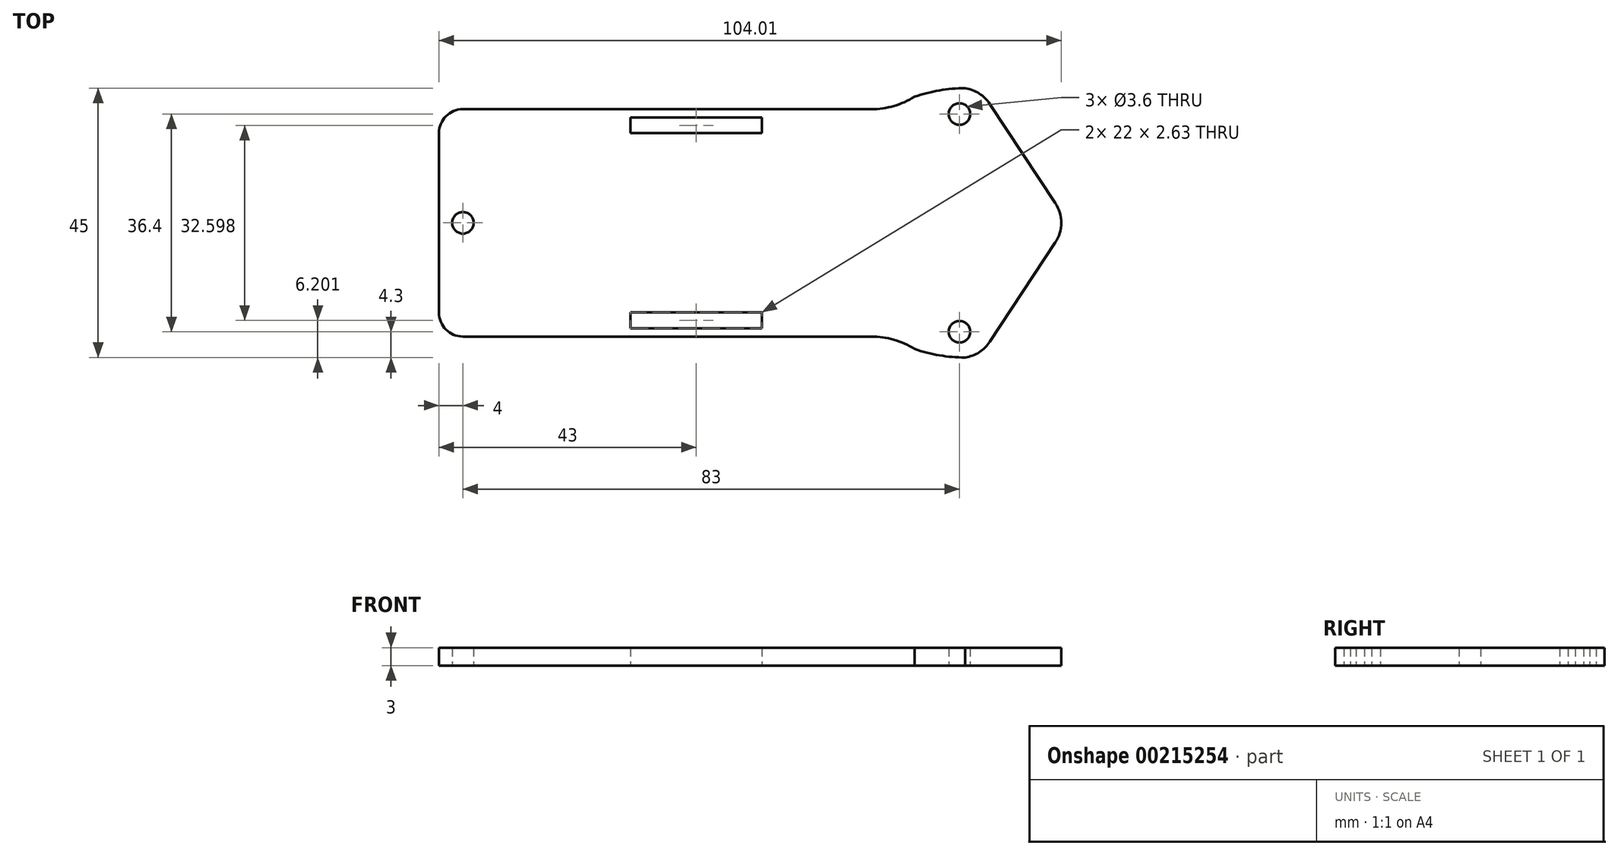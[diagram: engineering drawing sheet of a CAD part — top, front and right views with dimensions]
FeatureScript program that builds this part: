
annotation { "Feature Type Name" : "Feature", "Feature Type Description" : "" }
export const myFeature = defineFeature(function(context is Context, id is Id, definition is map)
    precondition{}
    {
        {
            var Q0;
            Q0=qCreatedBy(makeId("Top.planeOp"),FACE);
            var sketch = newSketch(context, id + "F0", { "sketchPlane" : qUnion([Q0])});
            skLineSegment(sketch, "E0.bottom", {"start": v(-18.2, -18.2) * mm, "end": v(18.2, -18.2) * mm, "construction": true});
            skLineSegment(sketch, "E0.top", {"start": v(-18.2, 18.2) * mm, "end": v(18.2, 18.2) * mm, "construction": true});
            skLineSegment(sketch, "E0.left", {"start": v(-18.2, -18.2) * mm, "end": v(-18.2, 18.2) * mm, "construction": true});
            skLineSegment(sketch, "E0.right", {"start": v(18.2, -18.2) * mm, "end": v(18.2, 18.2) * mm, "construction": true});
            skPoint(sketch, "E0.middle", {"position": v(0, 0) * mm});
            skCircle(sketch, "E1", {"center": v(-18.2, 18.2) * mm, "radius": 1.8 * mm});
            skCircle(sketch, "E2.MirrorC", {"center": v(-18.2, -18.2) * mm, "radius": 1.8 * mm});
            skPoint(sketch, "E3.right.end.orphan", {"position": v(80.8, 22.5) * mm});
            skPoint(sketch, "E4.orphan", {"position": v(80.8, -22.5) * mm});
            skLineSegment(sketch, "E5", {"start": v(-101.2, 19) * mm, "end": v(-70.85, 19) * mm});
            skLineSegment(sketch, "E6.MirrorCS", {"start": v(-101.2, -19) * mm, "end": v(-70.85, -19) * mm});
            skPoint(sketch, "E7.orphan", {"position": v(-80.8, 22.5) * mm});
            skPoint(sketch, "E8.orphan", {"position": v(-80.8, -22.5) * mm});
            skLineSegment(sketch, "E9.bottom", {"start": v(-73.2, -17.61) * mm, "end": v(-51.2, -17.61) * mm});
            skLineSegment(sketch, "E9.top", {"start": v(-73.2, -14.99) * mm, "end": v(-51.2, -14.99) * mm});
            skLineSegment(sketch, "E9.left", {"start": v(-73.2, -17.61) * mm, "end": v(-73.2, -14.99) * mm});
            skLineSegment(sketch, "E9.right", {"start": v(-51.2, -17.61) * mm, "end": v(-51.2, -14.99) * mm});
            skPoint(sketch, "E9.middle", {"position": v(-62.2, -16.3) * mm});
            skLineSegment(sketch, "E10.MirrorCS", {"start": v(-73.2, 14.99) * mm, "end": v(-51.2, 14.99) * mm});
            skLineSegment(sketch, "E11.MirrorCS", {"start": v(-73.2, 17.61) * mm, "end": v(-51.2, 17.61) * mm});
            skLineSegment(sketch, "E12.MirrorCS", {"start": v(-51.2, 17.61) * mm, "end": v(-51.2, 14.99) * mm});
            skLineSegment(sketch, "E13.MirrorCS", {"start": v(-73.2, 17.61) * mm, "end": v(-73.2, 14.99) * mm});
            skLineSegment(sketch, "E14", {"start": v(-105.2, 15) * mm, "end": v(-105.2, -15) * mm});
            skPoint(sketch, "E15.visualSharp", {"position": v(-105.2, 19) * mm});
            skArc(sketch, "E15.filletArc", {"start": v(-101.2, 19) * mm, "mid": v(-104.03, 17.83) * mm, "end": v(-105.2, 15) * mm});
            skPoint(sketch, "E16.visualSharp", {"position": v(-105.2, -19) * mm});
            skArc(sketch, "E16.filletArc", {"start": v(-105.2, -15) * mm, "mid": v(-104.03, -17.83) * mm, "end": v(-101.2, -19) * mm});
            skCircle(sketch, "E17", {"center": v(-101.2, 0) * mm, "radius": 1.8 * mm});
            skPoint(sketch, "E17.centerSnap0", {"position": v(-105.2, 0) * mm});
            skLineSegment(sketch, "E18", {"start": v(-70.85, 19) * mm, "end": v(-32.93, 19) * mm});
            skArc(sketch, "E19", {"start": v(-32.93, 19) * mm, "mid": v(-29.17, 19.53) * mm, "end": v(-25.7, 21.08) * mm});
            skArc(sketch, "E20", {"start": v(-17.27, 22.5) * mm, "mid": v(-21.55, 22.14) * mm, "end": v(-25.7, 21.08) * mm});
            skArc(sketch, "E21.MirrorCS", {"start": v(-32.93, -19) * mm, "mid": v(-29.17, -19.53) * mm, "end": v(-25.7, -21.08) * mm});
            skArc(sketch, "E22.MirrorCS", {"start": v(-17.27, -22.5) * mm, "mid": v(-21.55, -22.14) * mm, "end": v(-25.7, -21.08) * mm});
            skLineSegment(sketch, "E23", {"start": v(-70.85, -19) * mm, "end": v(-32.93, -19) * mm});
            skLineSegment(sketch, "E24", {"start": v(-51.2, 14.99) * mm, "end": v(-51.2, -14.99) * mm, "construction": true});
            skLineSegment(sketch, "E25", {"start": v(-105.2, 0) * mm, "end": v(-0.2, 0) * mm, "construction": true});
            skLineSegment(sketch, "E26", {"start": v(-13.12, 19.87) * mm, "end": v(-2.18, 3.3) * mm});
            skLineSegment(sketch, "E27.MirrorCS", {"start": v(-13.12, -19.87) * mm, "end": v(-2.18, -3.3) * mm});
            skArc(sketch, "E28", {"start": v(-13.12, 19.87) * mm, "mid": v(-14.91, 21.63) * mm, "end": v(-17.27, 22.5) * mm});
            skArc(sketch, "E29.MirrorCS", {"start": v(-13.12, -19.87) * mm, "mid": v(-14.91, -21.63) * mm, "end": v(-17.27, -22.5) * mm});
            skArc(sketch, "E30.filletArc", {"start": v(-2.18, -3.3) * mm, "mid": v(-1.19, 0) * mm, "end": v(-2.18, 3.3) * mm});
            skSolve(sketch);
        }
        {
            var Q0;
            Q0=makeQuery(id+"F0.imprint","IMPRINT",FACE,{"disambiguationData":[TD([[makeQuery(id+"F0.imprint","IMPRINT",EDGE,{"derivedFrom":sQuery(id+"F0.wireOp",EDGE,"E1")}),-1.0]])]});
            extrude(context, id + "F1", {"entities" : qUnion([Q0]), "depth" : 3 * mm});
        }
    });
